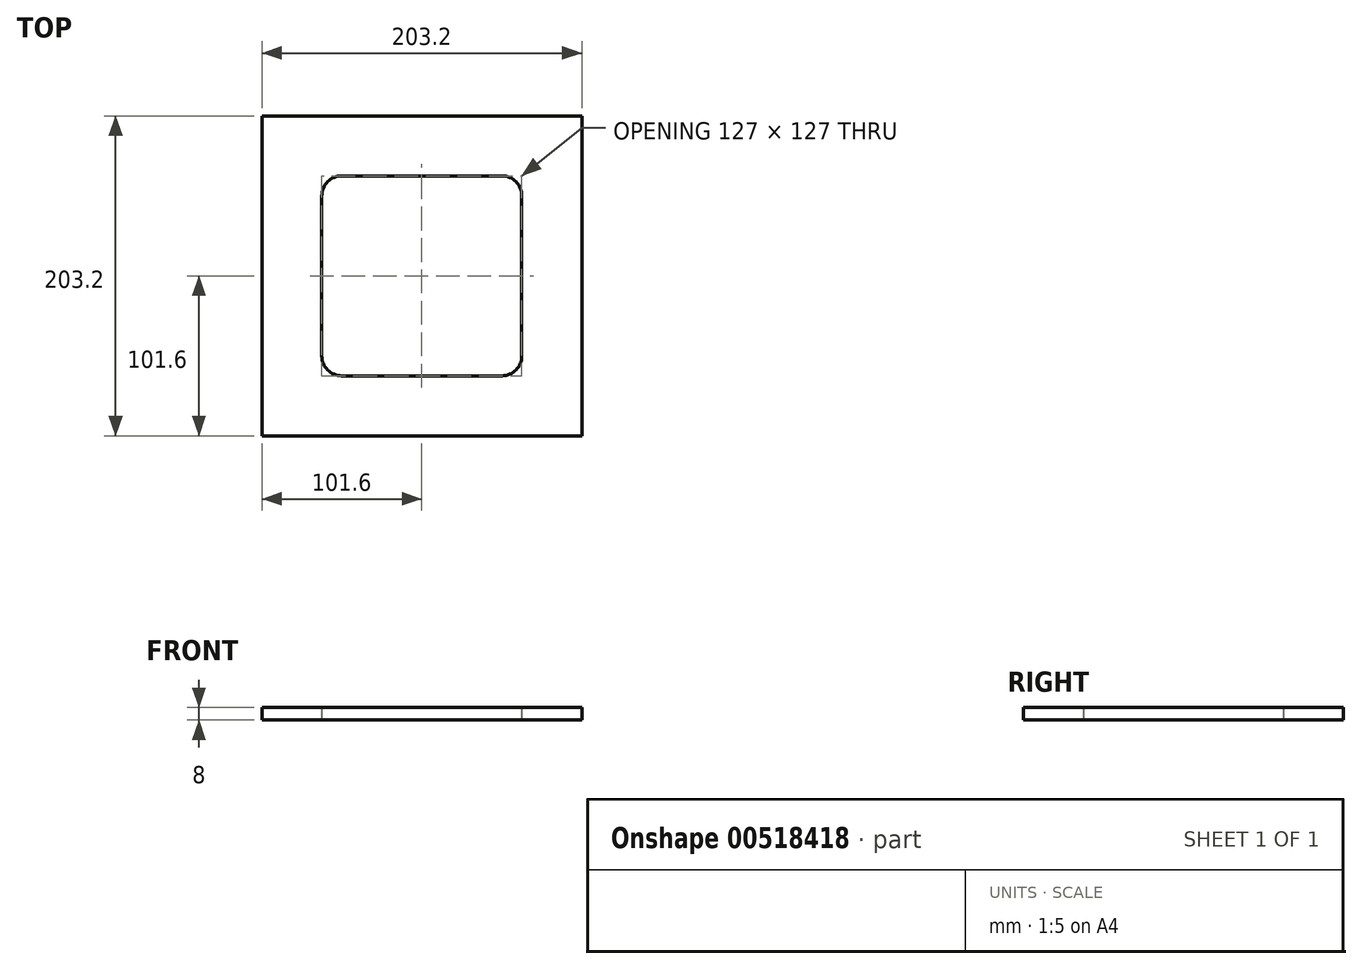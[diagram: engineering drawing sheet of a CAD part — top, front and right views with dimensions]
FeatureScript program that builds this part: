
annotation { "Feature Type Name" : "Feature", "Feature Type Description" : "" }
export const myFeature = defineFeature(function(context is Context, id is Id, definition is map)
    precondition{}
    {
        {
            assignVariable(context, id + "F0", {"name" : "CinderBlockHeight", "anyValue" : 8});
        }
        {
            var Q0;
            Q0=qCreatedBy(makeId("Top.planeOp"),FACE);
            var sketch = newSketch(context, id + "F1", { "sketchPlane" : qUnion([Q0])});
            skLineSegment(sketch, "E0.bottom", {"start": v(101.6, 101.6) * mm, "end": v(-101.6, 101.6) * mm});
            skLineSegment(sketch, "E0.top", {"start": v(101.6, -101.6) * mm, "end": v(-101.6, -101.6) * mm});
            skLineSegment(sketch, "E0.left", {"start": v(101.6, 101.6) * mm, "end": v(101.6, -101.6) * mm});
            skLineSegment(sketch, "E0.right", {"start": v(-101.6, 101.6) * mm, "end": v(-101.6, -101.6) * mm});
            skPoint(sketch, "E0.middle", {"position": v(0, 0) * mm});
            skLineSegment(sketch, "E1.0", {"start": v(50.8, 63.5) * mm, "end": v(-50.8, 63.5) * mm});
            skLineSegment(sketch, "E1.1", {"start": v(63.5, 50.8) * mm, "end": v(63.5, -50.8) * mm});
            skLineSegment(sketch, "E1.2", {"start": v(50.8, -63.5) * mm, "end": v(-50.8, -63.5) * mm});
            skLineSegment(sketch, "E1.3", {"start": v(-63.5, 50.8) * mm, "end": v(-63.5, -50.8) * mm});
            skPoint(sketch, "E2.visualSharp", {"position": v(-63.5, 63.5) * mm});
            skArc(sketch, "E2.filletArc", {"start": v(-50.8, 63.5) * mm, "mid": v(-59.78, 59.78) * mm, "end": v(-63.5, 50.8) * mm});
            skPoint(sketch, "E3.visualSharp", {"position": v(63.5, 63.5) * mm});
            skArc(sketch, "E3.filletArc", {"start": v(63.5, 50.8) * mm, "mid": v(59.78, 59.78) * mm, "end": v(50.8, 63.5) * mm});
            skPoint(sketch, "E4.visualSharp", {"position": v(63.5, -63.5) * mm});
            skArc(sketch, "E4.filletArc", {"start": v(50.8, -63.5) * mm, "mid": v(59.78, -59.78) * mm, "end": v(63.5, -50.8) * mm});
            skPoint(sketch, "E5.visualSharp", {"position": v(-63.5, -63.5) * mm});
            skArc(sketch, "E5.filletArc", {"start": v(-63.5, -50.8) * mm, "mid": v(-59.78, -59.78) * mm, "end": v(-50.8, -63.5) * mm});
            skSolve(sketch);
        }
        {
            var Q0;
            Q0=makeQuery(id+"F1.imprint","IMPRINT",FACE,{"disambiguationData":[TD([[makeQuery(id+"F1.imprint","IMPRINT",EDGE,{"derivedFrom":sQuery(id+"F1.wireOp",EDGE,"E0.bottom")}),1.0]])]});
            extrude(context, id + "F2", {"entities" : qUnion([Q0]), "depth" : (getVariable(context, 'CinderBlockHeight')) * mm, "offsetDistance" : 25.4 * mm});
        }
    });
